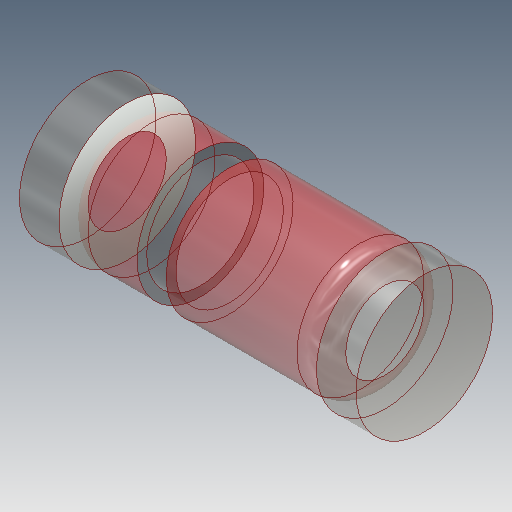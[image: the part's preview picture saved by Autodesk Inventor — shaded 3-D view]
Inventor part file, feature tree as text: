
AUTODESK INVENTOR PART (.ipt)
format: ipt  version: 2018 (Build 220112000, 112)  size: 216,064 bytes
history: native  units: mm
features: sketch x3, revolve x2, projected_geometry x2, extrude x1, mirror x1
ambient origin geometry x8: Origin, YZ Plane, XZ Plane, XY Plane, X Axis, Y Axis, Z Axis, Center Point
bodies: Solid1 (feature_tree)
feature tree (9):
  extrude  "Extrusion1"  Depth=3.45mm TaperAngle=0.0deg
  revolve  "Revolution1"  [1 undecoded]
  mirror  "Mirror1"
  revolve  "Revolution2"  Angle=90.0deg
  sketch  "Sketch1"  dims[d0=1.4mm d1=3.45mm d2=0.0mm]
  sketch  "Sketch2"  dims[d3=1.32mm d5=0.65mm]
  projected_geometry  "Projected Loop1"
  sketch  "Sketch3"  dims[d6=0.25mm d7=90.0deg d8=90.0deg d9=0.3mm d10=0.1mm d11=0.5mm d12=90.0deg]
  projected_geometry  "Projected Loop2"
note: 1 required parameter value undecoded (feature->parameter linkage not recoverable at this tier; creation-order binding heuristic only, values carry confidence <= 0.55)
